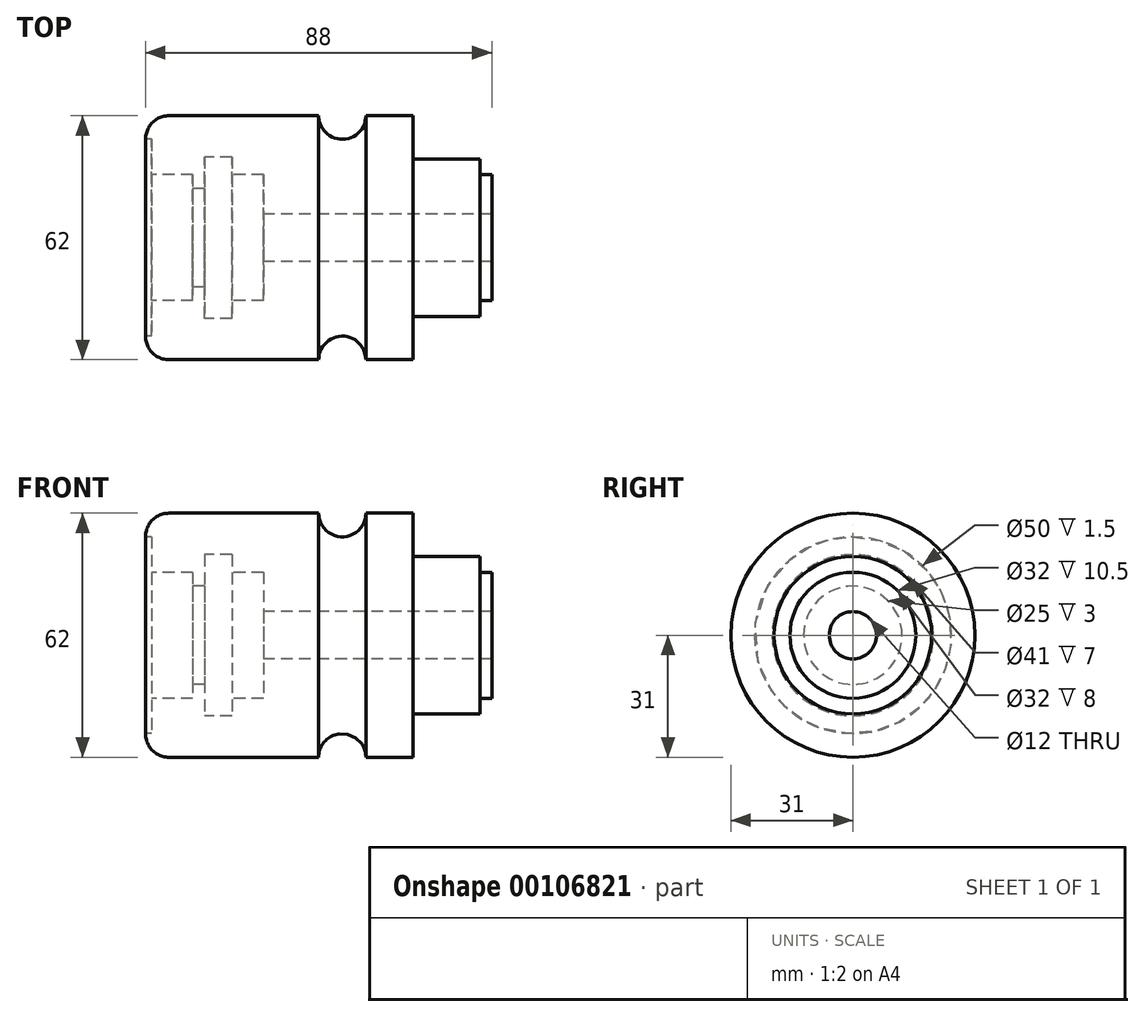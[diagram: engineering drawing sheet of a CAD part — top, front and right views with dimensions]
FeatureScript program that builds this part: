
annotation { "Feature Type Name" : "Feature", "Feature Type Description" : "" }
export const myFeature = defineFeature(function(context is Context, id is Id, definition is map)
    precondition{}
    {
        {
            var Q0;
            Q0=qCreatedBy(makeId("Front.planeOp"),FACE);
            var sketch = newSketch(context, id + "F0", { "sketchPlane" : qUnion([Q0])});
            skLineSegment(sketch, "E0", {"start": v(1.5, 16) * mm, "end": v(1.5, 25) * mm});
            skLineSegment(sketch, "E1", {"start": v(1.5, 25) * mm, "end": v(0, 25) * mm});
            skLineSegment(sketch, "E2", {"start": v(0, 25) * mm, "end": v(0, 25) * mm});
            skLineSegment(sketch, "E3", {"start": v(6, 31) * mm, "end": v(44, 31) * mm});
            skArc(sketch, "E4", {"start": v(44, 31) * mm, "mid": v(50, 25) * mm, "end": v(56, 31) * mm});
            skLineSegment(sketch, "E5", {"start": v(56, 31) * mm, "end": v(68, 31) * mm});
            skLineSegment(sketch, "E6", {"start": v(68, 31) * mm, "end": v(68, 20) * mm});
            skLineSegment(sketch, "E7", {"start": v(68, 20) * mm, "end": v(85, 20) * mm});
            skLineSegment(sketch, "E8", {"start": v(85, 20) * mm, "end": v(85, 16) * mm});
            skLineSegment(sketch, "E9", {"start": v(85, 16) * mm, "end": v(88, 16) * mm});
            skLineSegment(sketch, "E10", {"start": v(88, 16) * mm, "end": v(88, 6) * mm});
            skLineSegment(sketch, "E11", {"start": v(88, 6) * mm, "end": v(30, 6) * mm});
            skLineSegment(sketch, "E12", {"start": v(30, 6) * mm, "end": v(30, 16) * mm});
            skLineSegment(sketch, "E13", {"start": v(30, 16) * mm, "end": v(22, 16) * mm});
            skLineSegment(sketch, "E14", {"start": v(22, 16) * mm, "end": v(22, 20.5) * mm});
            skLineSegment(sketch, "E15", {"start": v(22, 20.5) * mm, "end": v(15, 20.5) * mm});
            skLineSegment(sketch, "E16", {"start": v(15, 20.5) * mm, "end": v(15, 12.5) * mm});
            skLineSegment(sketch, "E17", {"start": v(15, 12.5) * mm, "end": v(12, 12.5) * mm});
            skLineSegment(sketch, "E18", {"start": v(12, 12.5) * mm, "end": v(12, 16) * mm});
            skLineSegment(sketch, "E19", {"start": v(12, 16) * mm, "end": v(1.5, 16) * mm});
            skLineSegment(sketch, "E20", {"start": v(0, 0) * mm, "end": v(87.7, 0) * mm, "construction": true});
            skPoint(sketch, "E21.visualSharp", {"position": v(0, 31) * mm});
            skArc(sketch, "E21.filletArc", {"start": v(6, 31) * mm, "mid": v(1.76, 29.24) * mm, "end": v(0, 25) * mm});
            skSolve(sketch);
        }
        {
            var Q0;
            Q0=makeQuery(id+"F0.imprint","IMPRINT",FACE,{"disambiguationData":[TD([[makeQuery(id+"F0.imprint","IMPRINT",EDGE,{"derivedFrom":sQuery(id+"F0.wireOp",EDGE,"E0")}),-1.0]])]});
            var Q1;
            Q1=sQuery(id+"F0.wireOp",EDGE,"E20");
            revolve(context, id + "F1", {"entities" : qUnion([Q0]), "axis" : qUnion([Q1]), "revolveType" : RevolveType.FULL});
        }
    });
